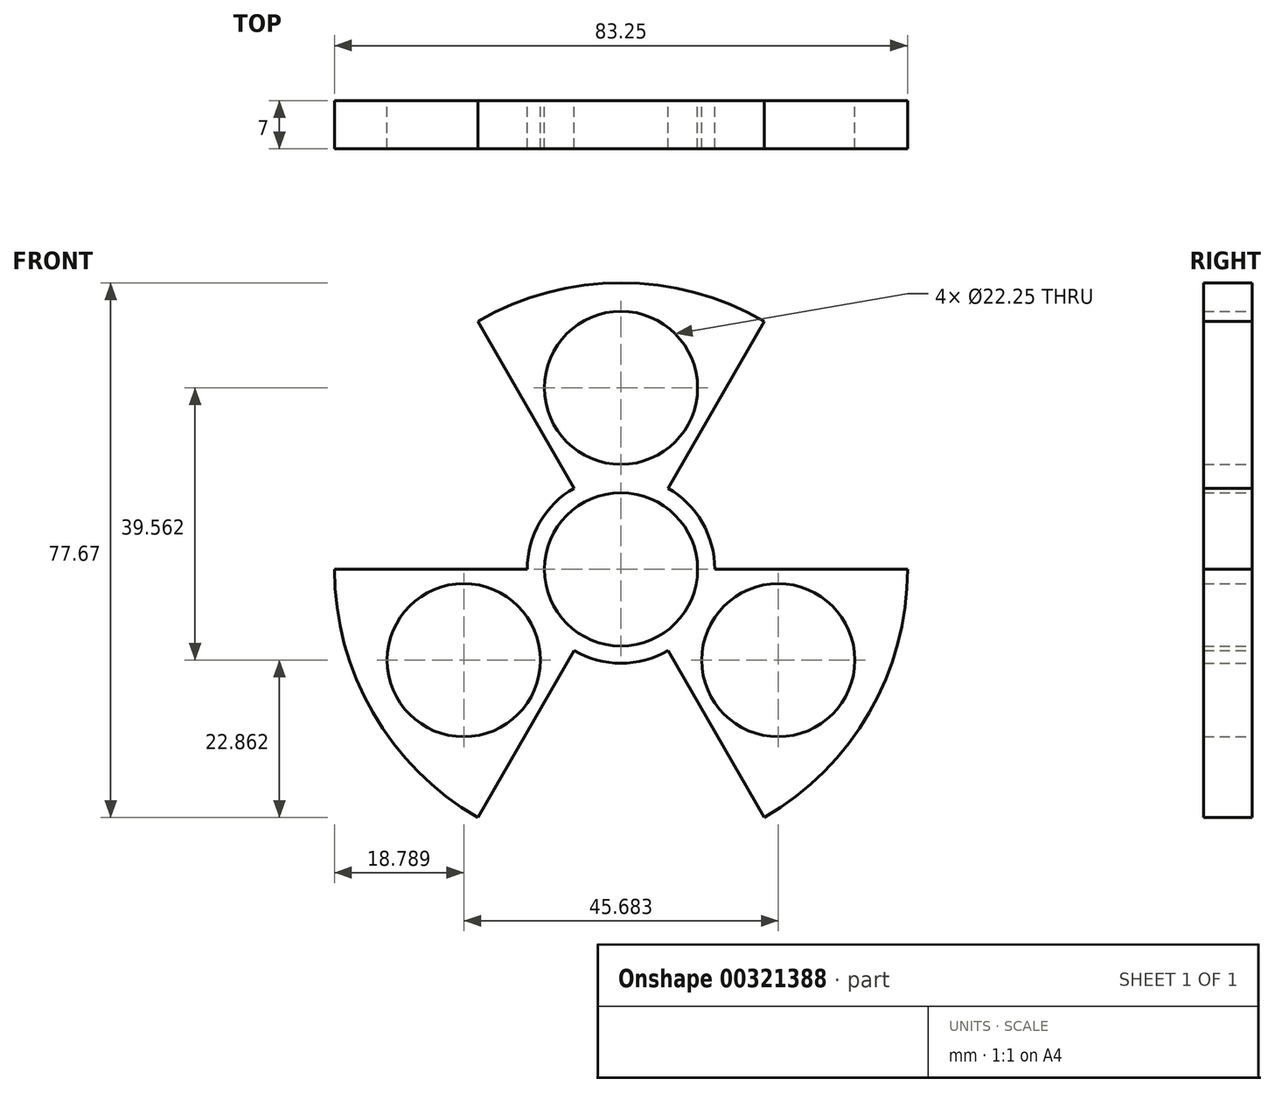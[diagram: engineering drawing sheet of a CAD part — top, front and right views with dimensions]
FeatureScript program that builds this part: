
annotation { "Feature Type Name" : "Feature", "Feature Type Description" : "" }
export const myFeature = defineFeature(function(context is Context, id is Id, definition is map)
    precondition{}
    {
        {
            var Q0;
            Q0=qCreatedBy(makeId("Front.planeOp"),FACE);
            var sketch = newSketch(context, id + "F0", { "sketchPlane" : qUnion([Q0])});
            skCircle(sketch, "E0", {"center": v(0, 0) * mm, "radius": 11.12 * mm});
            skCircle(sketch, "E1", {"center": v(0, 0) * mm, "radius": 13.62 * mm});
            skLineSegment(sketch, "E2", {"start": v(0, 0) * mm, "end": v(5.56, 9.63) * mm, "construction": true});
            skLineSegment(sketch, "E3", {"start": v(0, 0) * mm, "end": v(-5.56, 9.63) * mm, "construction": true});
            skLineSegment(sketch, "E4", {"start": v(-5.56, 9.63) * mm, "end": v(-6.81, 11.8) * mm, "construction": true});
            skLineSegment(sketch, "E5", {"start": v(5.56, 9.63) * mm, "end": v(6.81, 11.8) * mm, "construction": true});
            skLineSegment(sketch, "E6", {"start": v(6.81, 11.8) * mm, "end": v(20.81, 36.05) * mm});
            skLineSegment(sketch, "E7", {"start": v(-6.81, 11.8) * mm, "end": v(-20.81, 36.05) * mm});
            skArc(sketch, "E8", {"start": v(-20.81, 36.05) * mm, "mid": v(0, 41.62) * mm, "end": v(20.81, 36.05) * mm});
            skPoint(sketch, "E9", {"position": v(0, 26.38) * mm});
            skCircle(sketch, "E10", {"center": v(0, 26.38) * mm, "radius": 11.12 * mm});
            skPoint(sketch, "E11", {"position": v(0, 41.62) * mm});
            skPoint(sketch, "E12", {"position": v(0, 11.12) * mm});
            skPoint(sketch, "E13", {"position": v(0, 37.5) * mm});
            skPoint(sketch, "E14", {"position": v(0, 15.25) * mm});
            skCircle(sketch, "E15.1.0", {"center": v(-22.84, -13.19) * mm, "radius": 11.12 * mm});
            skArc(sketch, "E15.1.1", {"start": v(-20.81, -36.05) * mm, "mid": v(-36.05, -20.81) * mm, "end": v(-41.63, 0) * mm});
            skLineSegment(sketch, "E15.1.2", {"start": v(-6.81, -11.8) * mm, "end": v(-20.81, -36.05) * mm});
            skLineSegment(sketch, "E15.1.3", {"start": v(-13.62, 0) * mm, "end": v(-41.63, 0) * mm});
            skCircle(sketch, "E15.2.0", {"center": v(22.84, -13.19) * mm, "radius": 11.12 * mm});
            skArc(sketch, "E15.2.1", {"start": v(41.62, 0) * mm, "mid": v(36.05, -20.81) * mm, "end": v(20.81, -36.05) * mm});
            skLineSegment(sketch, "E15.2.2", {"start": v(13.62, 0) * mm, "end": v(41.63, 0) * mm});
            skLineSegment(sketch, "E15.2.3", {"start": v(6.81, -11.8) * mm, "end": v(20.81, -36.05) * mm});
            skSolve(sketch);
        }
        {
            var Q0;
            Q0 = qSketchRegion(id + "F0", true);
            extrude(context, id + "F1", {"entities" : qUnion([Q0]), "depth" : 7 * mm});
        }
    });
